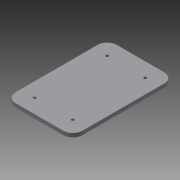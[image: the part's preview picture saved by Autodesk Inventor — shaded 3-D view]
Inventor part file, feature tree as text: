
AUTODESK INVENTOR PART (.ipt)
format: ipt  version: 2013 (Build 170138000, 138)  size: 110,592 bytes
history: native  units: mm
features: sketch x2, hole x2, mirror x2, extrude x1, fillet x1
ambient origin geometry x8: Origin, YZ Plane, XZ Plane, XY Plane, X Axis, Y Axis, Z Axis, Center Point
bodies: Solid1 (feature_tree)
feature tree (8):
  sketch  "Sketch1"  dims[d0=76.0mm d2=40.0mm]
  extrude  "Extrusion1"  Depth=40.0mm
  hole  "Hole1"  [1 undecoded]
  hole  "Hole2"  [1 undecoded]
  mirror  "Mirror1"
  mirror  "Mirror2"
  fillet  "Fillet1"  Radius=15.0mm
  sketch  "Sketch2"  dims[d3=15.0mm d4=15.0mm d5=15.0mm d6=15.0mm d7=4.0mm d8=0.0mm d9=12.0mm d10=6.0mm d11=4.0mm d12=2.0mm d13=90.0deg d14=2.0mm d15=0.0mm d43=10.0mm d44=10.0mm d18=3.1mm d19=6.0mm d20=4.0mm d21=2.0mm d22=90.0deg d23=3.0mm d24=0.0mm d25=10.0mm]
note: 2 required parameter values undecoded (feature->parameter linkage not recoverable at this tier; creation-order binding heuristic only, values carry confidence <= 0.55)
